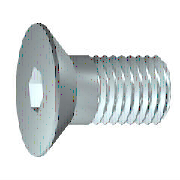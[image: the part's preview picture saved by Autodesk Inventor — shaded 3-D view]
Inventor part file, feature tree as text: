
AUTODESK INVENTOR PART (.ipt)
format: ipt  version: 2024.2 (Build 282272000, 272)  size: 197,120 bytes
history: native  units: mm (DEFAULTED — no unit token found)
features: other x4, sketch x1, fillet x1, chamfer x1
ambient origin geometry x8: Origin, YZ Plane, XZ Plane, XY Plane, X Axis, Y Axis, Z Axis, Center Point
bodies: Solid1 (feature_tree)
feature tree (7):
  sketch  "Sketch1"  dims[d2=3.0mm d3=3.0mm d4=1.5mm d5=1.5mm d6=8.0mm d7=6.0mm d8=360.0deg d9=0.0mm d10=2.0mm d11=2.0mm d12=120.0deg d13=120.0deg d14=120.0deg d15=120.0deg d16=1.2mm d17=0.0mm d18=0.1mm d19=0.25mm d20=45.0deg d22=0.0mm d23=0.0mm d35=0.0mm d37=0.0mm d38=0.0mm d39=0.25mm d40=0.0mm d41=0.0mm d42=0.0mm d43=45.0deg]
  other  "WorkPoint1"
  fillet  "Fillet1"  [1 undecoded]
  chamfer  "Chamfer1"  Distance=3.0mm
  other  "MSC_A1"
  other  "MSC_PF1"
  other  "MSC_PT1"
note: 1 required parameter value undecoded (feature->parameter linkage not recoverable at this tier; creation-order binding heuristic only, values carry confidence <= 0.55)
